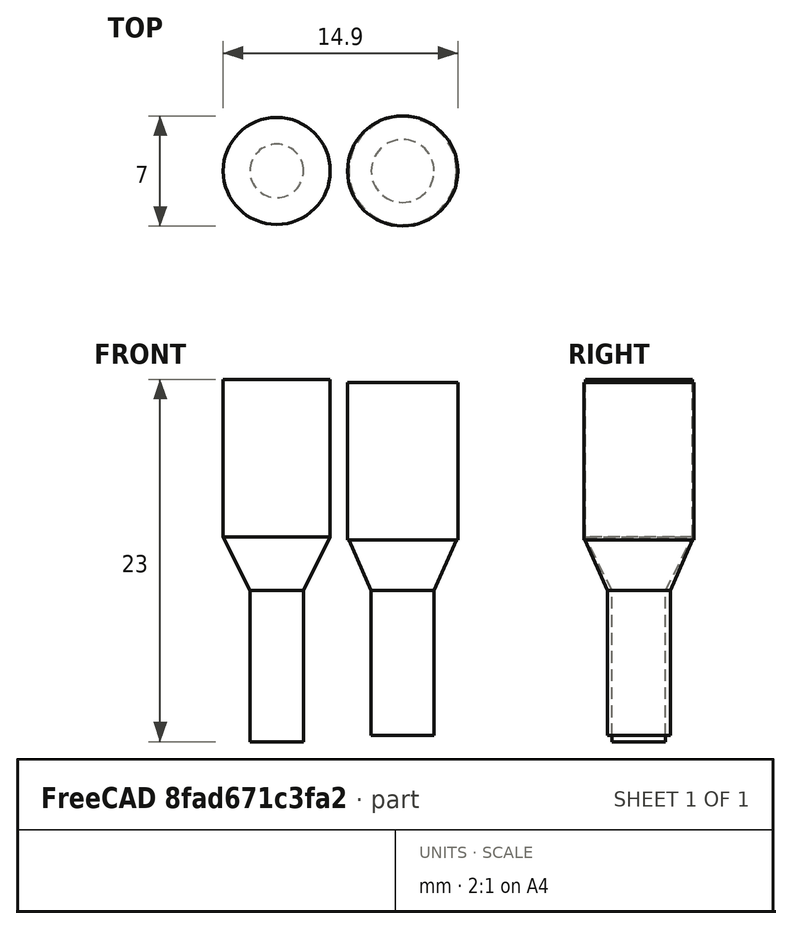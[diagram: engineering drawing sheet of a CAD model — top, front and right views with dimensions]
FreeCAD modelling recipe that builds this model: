
FCSTD DOCUMENT  (FreeCAD 0.19R24291 (Git))
Label: test-screws
License: All rights reserved
LicenseURL: http://en.wikipedia.org/wiki/All_rights_reserved
objects: Part::Cylinder×4, Part::Cone×2, Part::MultiFuse×2
note: 8 computed .brp shape members not serialized (recipe doc carries the construction recipe); baked Part::Feature solids carry a one-line shape summary decoded from their .brp

FEATURE [Part::Cone] Cone  label="pass-screw-head"
  Angle = 360
  AttacherType = Attacher::AttachEngine3D
  Height = 3.4
  Radius1 = 2
  Radius2 = 3.5
FEATURE [Part::Cylinder] Cylinder  label="pass-screw-thread"
  Angle = 360
  AttacherType = Attacher::AttachEngine3D
  Height = 9.2
  Placement = pos=(0,0,-9.2) rot=(0,0,1;0rad)
  Radius = 2
FEATURE [Part::Cylinder] Cylinder001  label="grab-screw-thread"
  Angle = 360
  AttacherType = Attacher::AttachEngine3D
  Height = 9.6
  Placement = pos=(0,0,-9.6) rot=(0,0,1;0rad)
  Radius = 1.7
FEATURE [Part::Cone] Cone001  label="grab-screw-head"
  Angle = 360
  AttacherType = Attacher::AttachEngine3D
  Height = 3.4
  Radius1 = 1.7
  Radius2 = 3.4
FEATURE [Part::Cylinder] Cylinder002  label="grab-screw-head-extension"
  Angle = 360
  AttacherType = Attacher::AttachEngine3D
  Height = 10
  Placement = pos=(0,0,3.4) rot=(0,0,1;0rad)
  Radius = 3.4
FEATURE [Part::Cylinder] Cylinder003  label="pass-screw-head-extension"
  Angle = 360
  AttacherType = Attacher::AttachEngine3D
  Height = 10
  Placement = pos=(0,0,3.2) rot=(0,0,1;0rad)
  Radius = 3.5
FEATURE [Part::MultiFuse] Fusion  label="bad-screw"
  Placement = pos=(8,0,0) rot=(0,0,1;0rad)
  Shapes = -> [Cylinder003,Cylinder,Cone]
FEATURE [Part::MultiFuse] Fusion001  label="grab-screw"
  Shapes = -> [Cylinder001,Cone001,Cylinder002]
